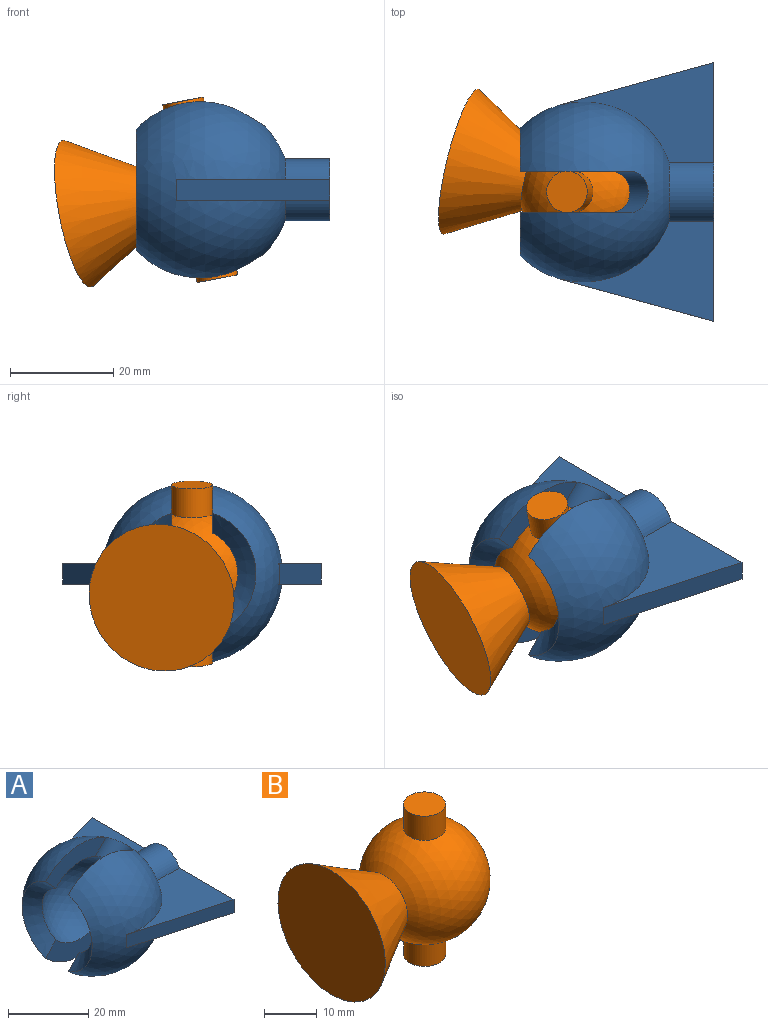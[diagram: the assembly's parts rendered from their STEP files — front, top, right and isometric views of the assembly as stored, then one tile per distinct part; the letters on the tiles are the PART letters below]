
ASSEMBLY  parts=2 mates=1
PART A: 23 faces, bbox 37.6x50.3x35.3 mm
  f0: cylinder r=6mm len=11.31mm, axis (-1,0,0), area 126.5mm2, adj f1,f4,f16,f20
  f1: sphere r=17.5mm, area 2530.7mm2, adj f0,f2,f5,f6,f7,f8,f9,f10
  f2: cone r=8.84mm half-angle=45deg, axis (-1,0,0), area 124.7mm2, adj f1,f3,f8,f9
  f3: sphere r=12.5mm, area 1372.4mm2, adj f2,f6,f7,f8,f9,f10,f11,f12
  f4: plane 50x12mm, normal (1,0,0), area 266mm2, adj f0,f5,f13,f14,f16,f19,f20,f21
  f5: cylinder r=6mm len=11.31mm, axis (-1,0,0), area 126.5mm2, adj f1,f4,f14,f19
  f6: cone r=8.84mm half-angle=45deg, axis (-1,0,0), area 124.7mm2, adj f1,f3,f7,f10
  f7: plane 21.52x9.42mm, normal (0,1,0), area 99.7mm2, adj f1,f3,f6,f11
  f8: plane 21.52x9.42mm, normal (0,-1,0), area 99.7mm2, adj f1,f2,f3,f11
  f9: plane 21.52x9.42mm, normal (0,-1,0), area 99.7mm2, adj f1,f2,f3,f12
  f10: plane 21.52x9.42mm, normal (0,1,0), area 99.7mm2, adj f1,f3,f6,f12
  f11: cylinder r=4mm len=8mm, axis (-0.71,0,0.71), area 65.4mm2, adj f1,f3,f7,f8
  f12: cylinder r=4mm len=8mm, axis (0.71,0,0.71), area 64.9mm2, adj f1,f3,f9,f10
  f13: plane 29.63x8.12mm, normal (-0.26,-0.96,0), area 122.9mm2, adj f4,f14,f15,f16,f17
  f14: plane 29.63x19.34mm, normal (0,0,1), area 258.6mm2, adj f1,f4,f5,f13,f15
  f15: plane 2.02x0.13mm, normal (-0.96,0.26,0), area 0.1mm2, adj f1,f13,f14
  f16: plane 29.63x19.34mm, normal (0,0,-1), area 258.6mm2, adj f0,f1,f4,f13,f17
  f17: plane 2.02x0.13mm, normal (-0.96,0.26,0), area 0.1mm2, adj f1,f13,f16
  f18: plane 2.02x0.13mm, normal (-0.96,-0.26,0), area 0.1mm2, adj f1,f19,f21
  f19: plane 29.63x19.34mm, normal (0,0,1), area 258.6mm2, adj f1,f4,f5,f18,f21
  f20: plane 29.63x19.34mm, normal (0,0,-1), area 258.6mm2, adj f0,f1,f4,f21,f22
  f21: plane 29.63x8.12mm, normal (-0.26,0.96,0), area 122.9mm2, adj f4,f18,f19,f20,f22
  f22: plane 2.02x0.13mm, normal (-0.96,-0.26,0), area 0.1mm2, adj f1,f20,f21
PART B: 7 faces, bbox 37.5x28.9x35 mm
  f0: sphere r=12.5mm, area 1728.7mm2, adj f1,f4,f5
  f1: cone r=6.25mm half-angle=30deg, axis (-1,0,0), area 1063.6mm2, adj f0,f2
  f2: plane 28.87x28.87mm, normal (-1,0,0), area 654.5mm2, adj f1
  f3: plane 8x8mm, normal (0,0,1), area 50.3mm2, adj f4
  f4: cylinder r=4mm len=8mm, axis (0,0,-1), area 142.2mm2, adj f0,f3
  f5: cylinder r=4mm len=8mm, axis (0,0,-1), area 142.2mm2, adj f0,f6
  f6: plane 8x8mm, normal (0,0,-1), area 50.3mm2, adj f5
PLACE A at identity fixed
PLACE B rot(axis=(-0.99,0.12,-0.09),178.7deg) t=(0,0,0)mm
MATE ball B.f4 <-> A.f1  axis (0.19,0,-0.98) through (0,0,0)mm
